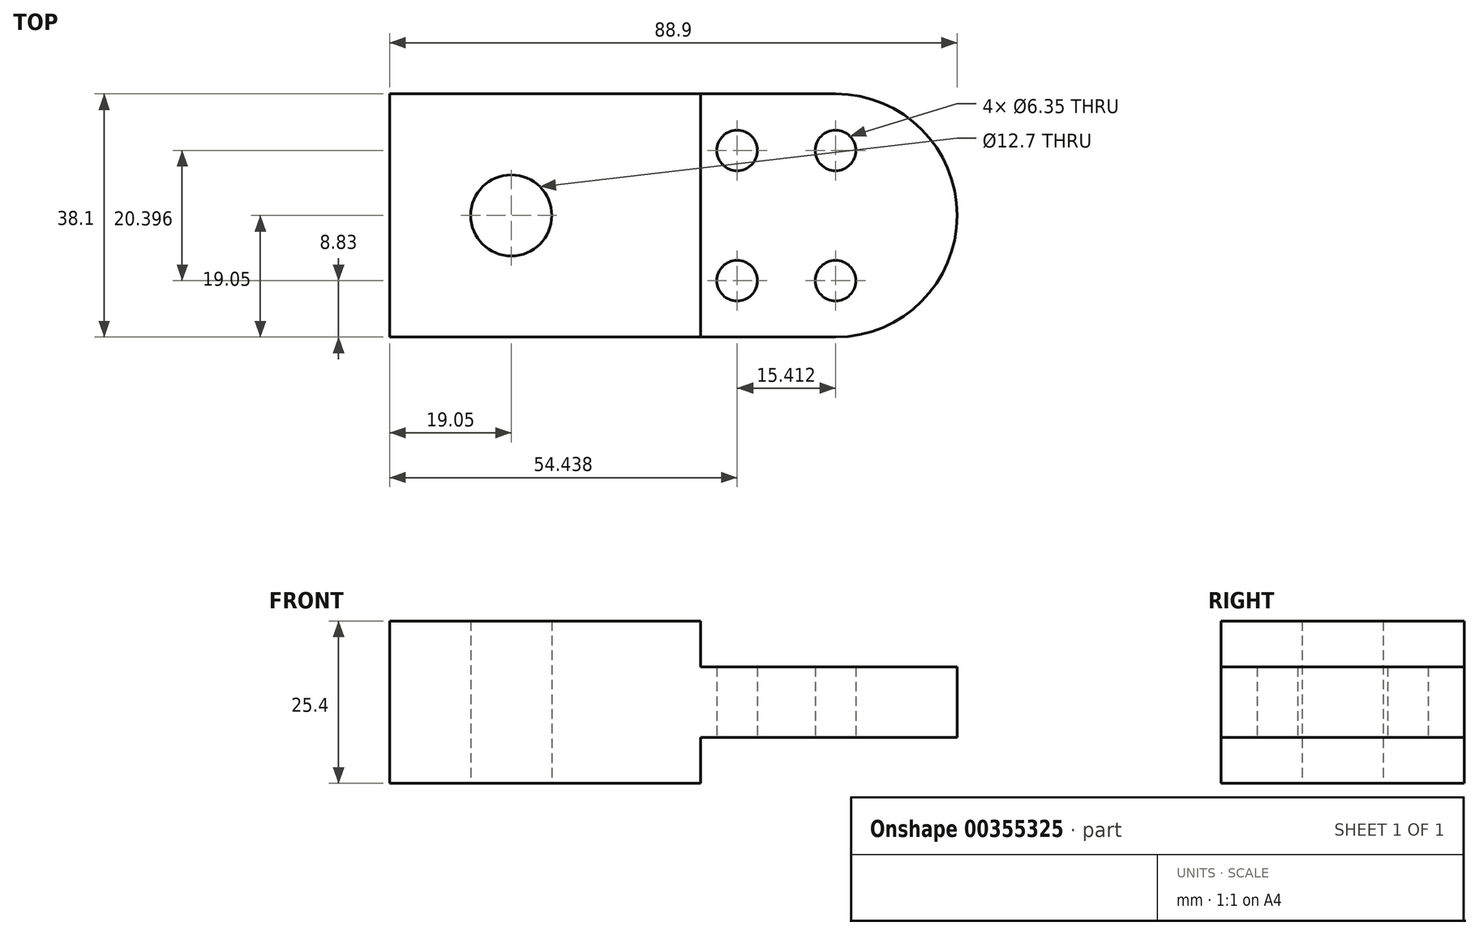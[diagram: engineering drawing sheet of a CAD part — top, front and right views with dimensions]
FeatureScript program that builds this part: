
annotation { "Feature Type Name" : "Feature", "Feature Type Description" : "" }
export const myFeature = defineFeature(function(context is Context, id is Id, definition is map)
    precondition{}
    {
        {
            var Q0;
            Q0=qCreatedBy(makeId("Top.planeOp"),FACE);
            var sketch = newSketch(context, id + "F0", { "sketchPlane" : qUnion([Q0])});
            skLineSegment(sketch, "E0.bottom", {"start": v(0, 38.1) * mm, "end": v(38.1, 38.1) * mm});
            skLineSegment(sketch, "E0.top", {"start": v(0, 0) * mm, "end": v(38.1, 0) * mm});
            skLineSegment(sketch, "E0.left", {"start": v(0, 38.1) * mm, "end": v(0, 0) * mm});
            skLineSegment(sketch, "E0.right", {"start": v(38.1, 38.1) * mm, "end": v(38.1, 0) * mm});
            skLineSegment(sketch, "E1", {"start": v(38.1, 38.1) * mm, "end": v(69.85, 38.1) * mm});
            skLineSegment(sketch, "E2", {"start": v(38.1, 0) * mm, "end": v(69.85, 0) * mm});
            skArc(sketch, "E3", {"start": v(69.85, 0) * mm, "mid": v(88.9, 19.05) * mm, "end": v(69.85, 38.1) * mm});
            skCircle(sketch, "E4", {"center": v(19.05, 19.05) * mm, "radius": 6.35 * mm});
            skPoint(sketch, "E4.centerSnap0", {"position": v(19.05, 38.1) * mm});
            skPoint(sketch, "E4.centerSnap1", {"position": v(0, 19.05) * mm});
            skCircle(sketch, "E5", {"center": v(54.44, 29.23) * mm, "radius": 3.18 * mm});
            skCircle(sketch, "E6", {"center": v(69.85, 29.23) * mm, "radius": 3.18 * mm});
            skCircle(sketch, "E7", {"center": v(54.44, 8.83) * mm, "radius": 3.18 * mm});
            skCircle(sketch, "E8", {"center": v(69.85, 8.83) * mm, "radius": 3.18 * mm});
            skSolve(sketch);
        }
        {
            var Q0;
            Q0=makeQuery(id+"F0.imprint","IMPRINT",FACE,{"disambiguationData":[TD([[makeQuery(id+"F0.imprint","IMPRINT",EDGE,{"derivedFrom":sQuery(id+"F0.wireOp",EDGE,"E0.bottom")}),-1.0]])]});
            var Q1;
            Q1=makeQuery(id+"F0.imprint","IMPRINT",FACE,{"disambiguationData":[TD([[makeQuery(id+"F0.imprint","IMPRINT",EDGE,{"derivedFrom":sQuery(id+"F0.wireOp",EDGE,"E0.right")}),1.0]])]});
            extrude(context, id + "F1", {"entities" : qUnion([Q0, Q1]), "depth" : 25.4 * mm});
        }
        {
            var Q0;
            Q0=makeQuery(id+"F1.opExtrude","SWEPT_FACE",FACE,{"disambiguationData":[OSD([sQuery(id+"F0.wireOp",EDGE,"E0.top"),sQuery(id+"F0.wireOp",EDGE,"E2")])]});
            var sketch = newSketch(context, id + "F2", { "sketchPlane" : qUnion([Q0])});
            skLineSegment(sketch, "E9.bottom", {"start": v(48.73, 25.4) * mm, "end": v(88.94, 25.4) * mm});
            skLineSegment(sketch, "E9.top", {"start": v(48.73, 18.2) * mm, "end": v(88.94, 18.2) * mm});
            skLineSegment(sketch, "E9.left", {"start": v(48.73, 25.4) * mm, "end": v(48.73, 18.2) * mm});
            skLineSegment(sketch, "E9.right", {"start": v(88.94, 25.4) * mm, "end": v(88.94, 18.2) * mm});
            skLineSegment(sketch, "E10.bottom", {"start": v(48.73, 0) * mm, "end": v(88.94, 0) * mm});
            skLineSegment(sketch, "E10.top", {"start": v(48.73, 7.2) * mm, "end": v(88.94, 7.2) * mm});
            skLineSegment(sketch, "E10.left", {"start": v(48.73, 0) * mm, "end": v(48.73, 7.2) * mm});
            skLineSegment(sketch, "E10.right", {"start": v(88.94, 0) * mm, "end": v(88.94, 7.2) * mm});
            skSolve(sketch);
        }
        {
            var Q0;
            {var subQ4=sQuery(id+"F2.wireOp",EDGE,"E9.left");Q0=makeQuery(id+"F2.imprint","IMPRINT",FACE,{"disambiguationData":[TD([[makeQuery(id+"F2.imprint","IMPRINT",EDGE,{"derivedFrom":subQ4}),1.0]])]});}
            var Q1;
            {var subQ3=sQuery(id+"F2.wireOp",EDGE,"E9.right");Q1=makeQuery(id+"F2.imprint","IMPRINT",FACE,{"disambiguationData":[TD([[makeQuery(id+"F2.imprint","IMPRINT",EDGE,{"derivedFrom":subQ3}),-1.0]])]});}
            var Q2;
            {var subQ4=sQuery(id+"F2.wireOp",EDGE,"E10.left");Q2=makeQuery(id+"F2.imprint","IMPRINT",FACE,{"disambiguationData":[TD([[makeQuery(id+"F2.imprint","IMPRINT",EDGE,{"derivedFrom":subQ4}),-1.0]])]});}
            var Q3;
            {var subQ3=sQuery(id+"F2.wireOp",EDGE,"E10.right");Q3=makeQuery(id+"F2.imprint","IMPRINT",FACE,{"disambiguationData":[TD([[makeQuery(id+"F2.imprint","IMPRINT",EDGE,{"derivedFrom":subQ3}),1.0]])]});}
            extrude(context, id + "F3", {"entities" : qUnion([Q0, Q1, Q2, Q3]), "operationType" : NewBodyOperationType.REMOVE, "endBound" : BoundingType.THROUGH_ALL, "oppositeDirection" : true, "depth" : 25.4 * mm});
        }
    });
